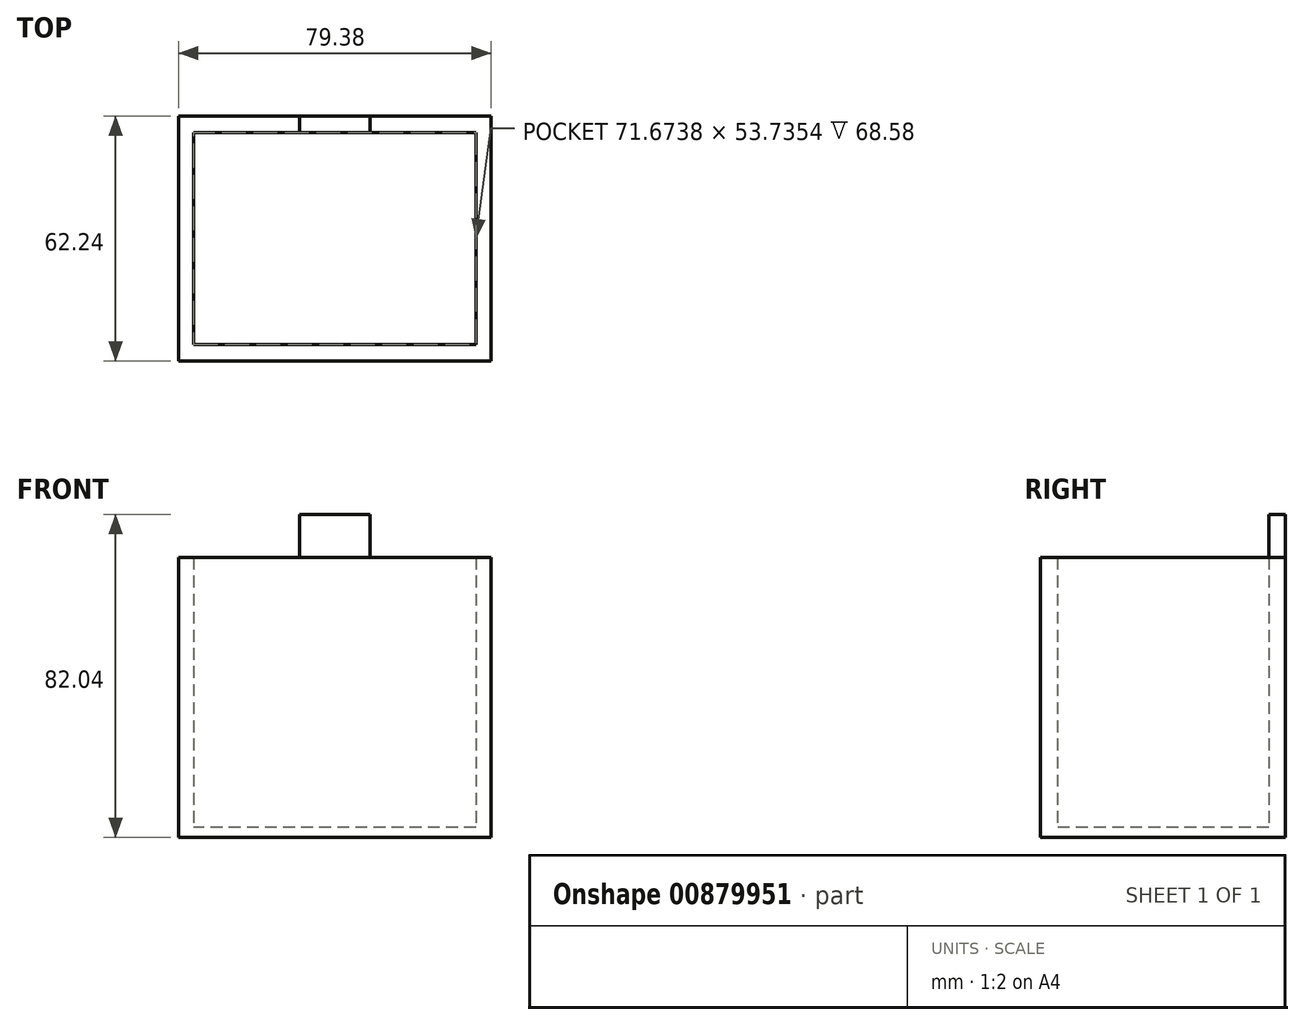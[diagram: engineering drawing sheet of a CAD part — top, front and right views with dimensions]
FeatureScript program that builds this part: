
annotation { "Feature Type Name" : "Feature", "Feature Type Description" : "" }
export const myFeature = defineFeature(function(context is Context, id is Id, definition is map)
    precondition{}
    {
        {
            var Q0;
            Q0=qCreatedBy(makeId("Top.planeOp"),FACE);
            var sketch = newSketch(context, id + "F0", { "sketchPlane" : qUnion([Q0])});
            skLineSegment(sketch, "E0.bottom", {"start": v(39.69, 31.12) * mm, "end": v(-39.69, 31.12) * mm});
            skLineSegment(sketch, "E0.top", {"start": v(39.69, -31.12) * mm, "end": v(-39.69, -31.12) * mm});
            skLineSegment(sketch, "E0.left", {"start": v(39.69, 31.12) * mm, "end": v(39.69, -31.12) * mm});
            skLineSegment(sketch, "E0.right", {"start": v(-39.69, 31.12) * mm, "end": v(-39.69, -31.12) * mm});
            skPoint(sketch, "E0.middle", {"position": v(0, 0) * mm});
            skLineSegment(sketch, "E1.bottom", {"start": v(35.84, 26.87) * mm, "end": v(-35.84, 26.87) * mm});
            skLineSegment(sketch, "E1.top", {"start": v(35.84, -26.87) * mm, "end": v(-35.84, -26.87) * mm});
            skLineSegment(sketch, "E1.left", {"start": v(35.84, 26.87) * mm, "end": v(35.84, -26.87) * mm});
            skLineSegment(sketch, "E1.right", {"start": v(-35.84, 26.87) * mm, "end": v(-35.84, -26.87) * mm});
            skLineSegment(sketch, "E2", {"start": v(0, 31.12) * mm, "end": v(0, -31.12) * mm});
            skLineSegment(sketch, "E3", {"start": v(8.97, 31.12) * mm, "end": v(8.97, 26.87) * mm});
            skLineSegment(sketch, "E4.MirrorCS", {"start": v(-8.97, 31.12) * mm, "end": v(-8.97, 26.87) * mm});
            skSolve(sketch);
        }
        {
            var Q0;
            {var subQ3=sQuery(id+"F0.wireOp",EDGE,"E0.left");Q0=makeQuery(id+"F0.imprint","IMPRINT",FACE,{"disambiguationData":[TD([[makeQuery(id+"F0.imprint","IMPRINT",EDGE,{"derivedFrom":subQ3}),-1.0]])]});}
            var Q1;
            {var subQ3=sQuery(id+"F0.wireOp",EDGE,"E0.right");Q1=makeQuery(id+"F0.imprint","IMPRINT",FACE,{"disambiguationData":[TD([[makeQuery(id+"F0.imprint","IMPRINT",EDGE,{"derivedFrom":subQ3}),1.0]])]});}
            extrude(context, id + "F1", {"entities" : qUnion([Q0, Q1]), "depth" : 71.12 * mm, "offsetDistance" : 25.4 * mm});
        }
        {
            var Q0;
            Q0=makeQuery(id+"F0.imprint","IMPRINT",FACE,{"disambiguationData":[TD([[makeQuery(id+"F0.imprint","IMPRINT",EDGE,{"derivedFrom":sQuery(id+"F0.wireOp",EDGE,"E1.bottom")}),1.0]])]});
            extrude(context, id + "F2", {"entities" : qUnion([Q0]), "operationType" : NewBodyOperationType.ADD, "depth" : 2.54 * mm, "offsetDistance" : 25.4 * mm});
        }
        {
            var Q0;
            {var subQ3=sQuery(id+"F0.wireOp",EDGE,"E4.MirrorCS");Q0=makeQuery(id+"F0.imprint","IMPRINT",FACE,{"disambiguationData":[TD([[makeQuery(id+"F0.imprint","IMPRINT",EDGE,{"derivedFrom":subQ3}),1.0]])]});}
            var Q1;
            {var subQ3=sQuery(id+"F0.wireOp",EDGE,"E3");Q1=makeQuery(id+"F0.imprint","IMPRINT",FACE,{"disambiguationData":[TD([[makeQuery(id+"F0.imprint","IMPRINT",EDGE,{"derivedFrom":subQ3}),-1.0]])]});}
            extrude(context, id + "F3", {"entities" : qUnion([Q0, Q1]), "operationType" : NewBodyOperationType.ADD, "depth" : 82.04 * mm, "offsetDistance" : 25.4 * mm});
        }
    });
